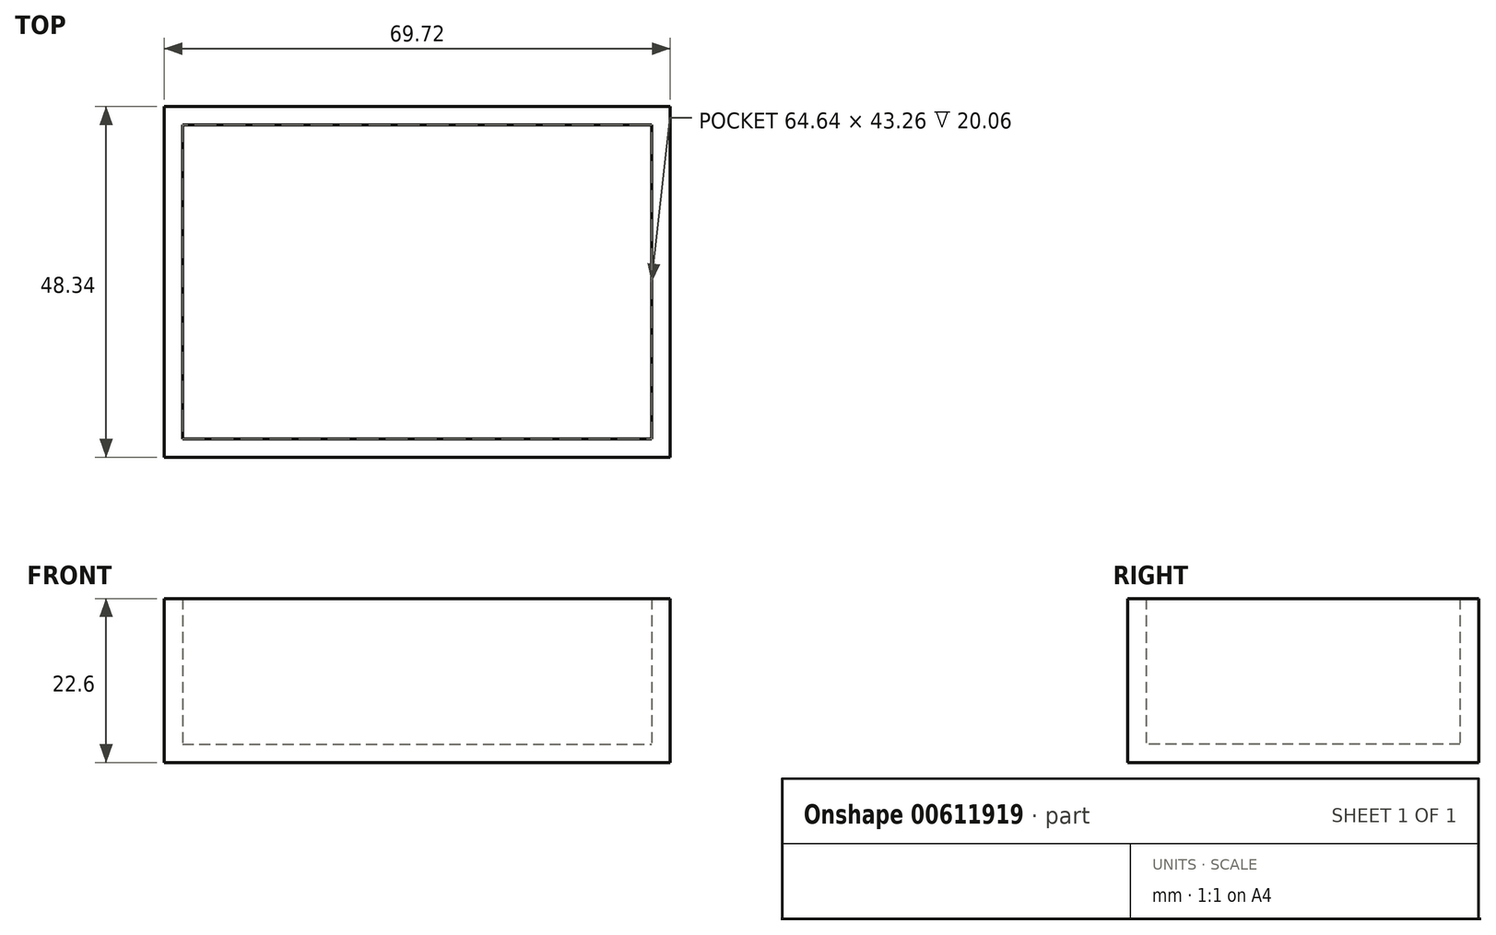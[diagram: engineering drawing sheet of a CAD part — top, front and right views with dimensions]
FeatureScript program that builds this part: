
annotation { "Feature Type Name" : "Feature", "Feature Type Description" : "" }
export const myFeature = defineFeature(function(context is Context, id is Id, definition is map)
    precondition{}
    {
        {
            var Q0;
            Q0=qCreatedBy(makeId("Top.planeOp"),FACE);
            var sketch = newSketch(context, id + "F0", { "sketchPlane" : qUnion([Q0])});
            skLineSegment(sketch, "E0.bottom", {"start": v(-35.17, 24.17) * mm, "end": v(34.55, 24.17) * mm});
            skLineSegment(sketch, "E0.top", {"start": v(-35.17, -24.17) * mm, "end": v(34.55, -24.17) * mm});
            skLineSegment(sketch, "E0.left", {"start": v(-35.17, 24.17) * mm, "end": v(-35.17, -24.17) * mm});
            skLineSegment(sketch, "E0.right", {"start": v(34.55, 24.17) * mm, "end": v(34.55, -24.17) * mm});
            skPoint(sketch, "E0.middle", {"position": v(-0.3, 0) * mm});
            skSolve(sketch);
        }
        {
            var Q0;
            Q0 = qSketchRegion(id + "F0", true);
            var Q1;
            Q1 = qConstructionFilter(qBodyType(qCreatedBy(id + "F0" ,EDGE), BodyType.WIRE), ConstructionObject.NO);
            extrude(context, id + "F1", {"entities" : qUnion([Q0]), "bodyType" : ToolBodyType.SURFACE, "surfaceEntities" : qUnion([Q1]), "depth" : 25.4 * mm, "offsetDistance" : 25.4 * mm});
        }
        {
            var Q0;
            Q0 = qSketchRegion(id + "F0", true);
            extrude(context, id + "F2", {"entities" : qUnion([Q0]), "flatOperationType" : FlatOperationType.REMOVE, "depth" : 22.6 * mm, "offsetDistance" : 25.4 * mm, "domain" : OperationDomain.MODEL});
        }
        {
            var Q0;
            Q0=makeQuery(id+"F2.opExtrude","CAP_FACE",FACE,{"disambiguationData":[OSD([sQuery(id+"F0.wireOp",EDGE,"E0.bottom"),sQuery(id+"F0.wireOp",EDGE,"E0.top"),sQuery(id+"F0.wireOp",EDGE,"E0.left"),sQuery(id+"F0.wireOp",EDGE,"E0.right")])],"isStart":false});
            shell(context, id + "F3", {"entities" : qUnion([Q0]), "thickness" : 2.54 * mm});
        }
    });
